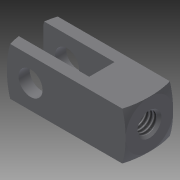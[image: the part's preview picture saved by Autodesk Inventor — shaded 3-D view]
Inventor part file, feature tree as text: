
AUTODESK INVENTOR PART (.ipt)
format: ipt  version: 2014 (Build 180170000, 170)  size: 190,464 bytes
history: native  units: in
note: dims shown in document units (in); Inventor stores cm internally (conversion verified against a paired STEP export)
features: other x126, sketch x7, hole x3, extrude x2, revolve x2
ambient origin geometry x8: Origin, YZ Plane, XZ Plane, XY Plane, X Axis, Y Axis, Z Axis, Center Point
bodies: Solid1 (feature_tree)
feature tree (140):
  extrude  "Extrusion1"  Depth=0.375in TaperAngle=0.0deg
  extrude  "Extrusion2"  TaperAngle=360.0deg  [1 undecoded]
  hole  "Hole1"  [1 undecoded]
  hole  "Hole2"  [1 undecoded]
  hole  "Hole3"  [1 undecoded]
  revolve  "Revolution1"  [1 undecoded]
  revolve  "Revolution2"  [1 undecoded]
  other  "dummy_XY"
  other  "dummy_YZ"
  other  "dummy_ZX"
  other  "dummy_X"
  other  "dummy_Y"
  other  "dummy_Z"
  other  "dummy_Center"
  other  "h1_XY"
  other  "h1_YZ"
  other  "h1_ZX"
  other  "h1_X"
  other  "h1_Y"
  other  "h1_Z"
  other  "h1_Center"
  other  "h2_XY"
  other  "h2_YZ"
  other  "h2_ZX"
  other  "h2_X"
  other  "h2_Y"
  other  "h2_Z"
  other  "h2_Center"
  other  "l1_XY"
  other  "l1_YZ"
  other  "l1_ZX"
  other  "l1_X"
  other  "l1_Y"
  other  "l1_Z"
  other  "l1_Center"
  other  "l11_XY"
  other  "l11_YZ"
  other  "l11_ZX"
  other  "l11_X"
  other  "l11_Y"
  other  "l11_Z"
  other  "l11_Center"
  other  "l12_XY"
  other  "l12_YZ"
  other  "l12_ZX"
  other  "l12_X"
  other  "l12_Y"
  other  "l12_Z"
  other  "l12_Center"
  other  "l2_XY"
  other  "l2_YZ"
  other  "l2_ZX"
  other  "l2_X"
  other  "l2_Y"
  other  "l2_Z"
  other  "l2_Center"
  other  "l21_XY"
  other  "l21_YZ"
  other  "l21_ZX"
  other  "l21_X"
  other  "l21_Y"
  other  "l21_Z"
  other  "l21_Center"
  other  "l22_XY"
  other  "l22_YZ"
  other  "l22_ZX"
  other  "l22_X"
  other  "l22_Y"
  other  "l22_Z"
  other  "l22_Center"
  other  "piston_rod_clevis_XY"
  other  "piston_rod_clevis_YZ"
  other  "piston_rod_clevis_ZX"
  other  "piston_rod_clevis_X"
  other  "piston_rod_clevis_Y"
  other  "piston_rod_clevis_Z"
  other  "piston_rod_clevis_Center"
  other  "rod_clevis_body_XY"
  other  "rod_clevis_body_YZ"
  other  "rod_clevis_body_ZX"
  other  "rod_clevis_body_X"
  other  "rod_clevis_body_Y"
  other  "rod_clevis_body_Z"
  other  "rod_clevis_body_Center"
  other  "th1_XY"
  other  "th1_YZ"
  other  "th1_ZX"
  other  "th1_X"
  other  "th1_Y"
  other  "th1_Z"
  other  "th1_Center"
  other  "th2_XY"
  other  "th2_YZ"
  other  "th2_ZX"
  other  "th2_X"
  other  "th2_Y"
  other  "th2_Z"
  other  "th2_Center"
  other  "to_cylinder_XY"
  other  "to_cylinder_YZ"
  other  "to_cylinder_ZX"
  other  "to_cylinder_X"
  other  "to_cylinder_Y"
  other  "to_cylinder_Z"
  other  "to_cylinder_Center"
  other  "w1_XY"
  other  "w1_YZ"
  other  "w1_ZX"
  other  "w1_X"
  other  "w1_Y"
  other  "w1_Z"
  other  "w1_Center"
  other  "w11_XY"
  other  "w11_YZ"
  other  "w11_ZX"
  other  "w11_X"
  other  "w11_Y"
  other  "w11_Z"
  other  "w11_Center"
  other  "w12_XY"
  other  "w12_YZ"
  other  "w12_ZX"
  other  "w12_X"
  other  "w12_Y"
  other  "w12_Z"
  other  "w12_Center"
  other  "w2_XY"
  other  "w2_YZ"
  other  "w2_ZX"
  other  "w2_X"
  other  "w2_Y"
  other  "w2_Z"
  other  "w2_Center"
  sketch  "Sketch_1"  dims[d0=0.375in d1=0.0in d2=0.375in d3=0.0in]
  sketch  "Sketch_2"  dims[d4=0.156in d5=0.31in d6=0.19in d7=0.25in d8=90.0deg d9=0.31in d10=0.0in]
  sketch  "Sketch3"  dims[d11=0.1562in d12=0.75in d13=0.375in d14=0.25in d15=0.5635in d16=0.065in d17=0.0in]
  sketch  "Sketch4"  dims[d18=0.19in d19=0.75in d20=0.375in d21=0.25in d22=0.5635in d23=0.375in d24=0.0in d25=360.0deg]
  sketch  "Sketch5"  dims[d26=360.0deg]
  sketch  "Sketch_9"
  sketch  "Sketch_10"
note: 6 required parameter values undecoded (feature->parameter linkage not recoverable at this tier; creation-order binding heuristic only, values carry confidence <= 0.55)
